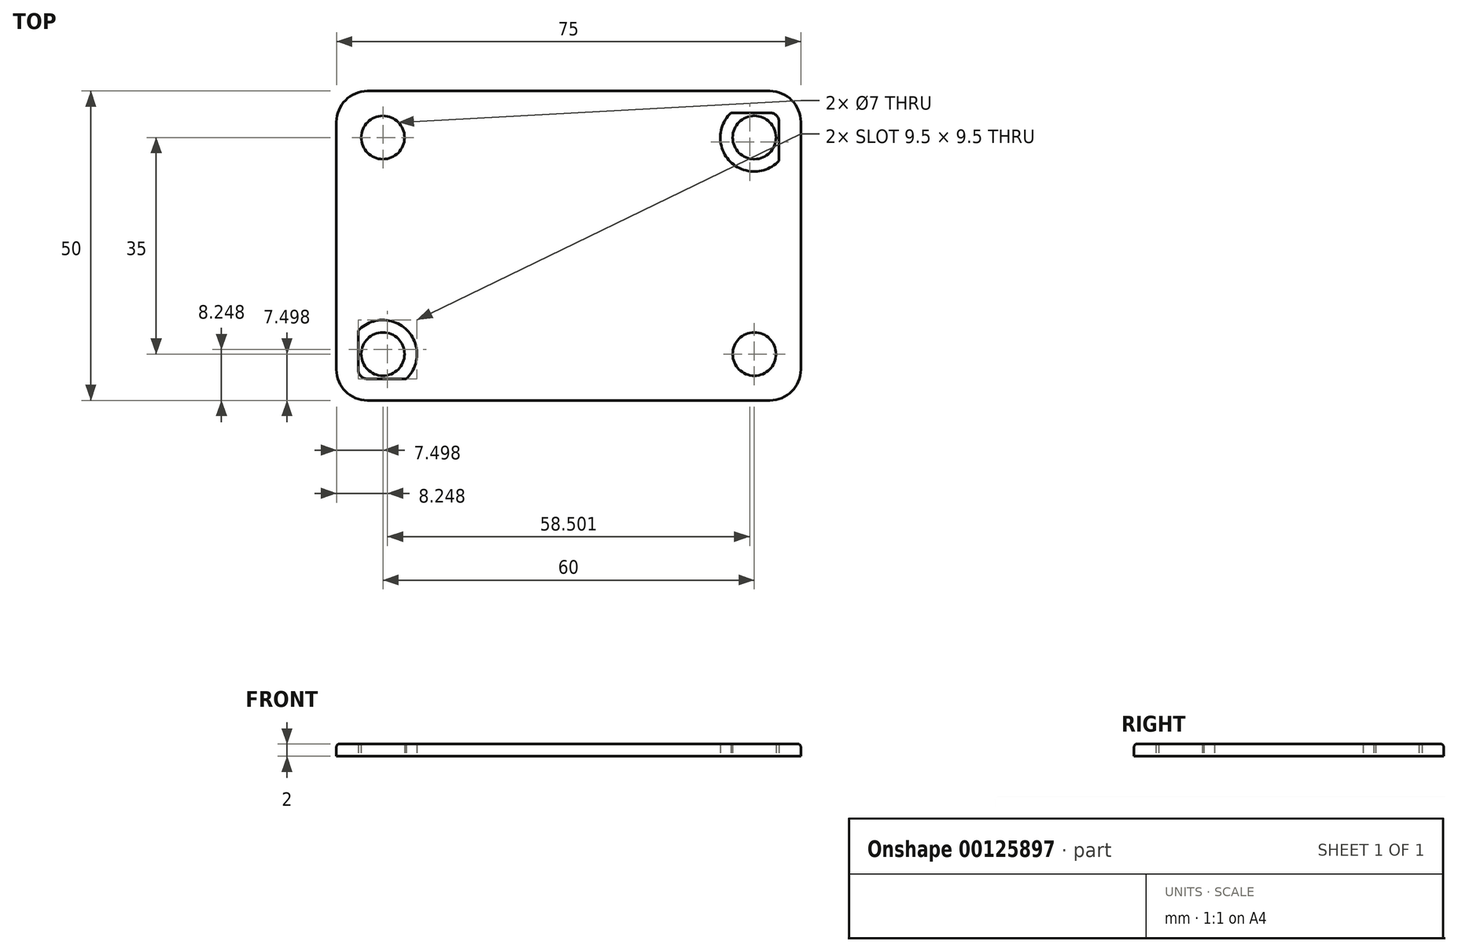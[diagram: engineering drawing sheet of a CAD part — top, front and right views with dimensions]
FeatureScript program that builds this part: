
annotation { "Feature Type Name" : "Feature", "Feature Type Description" : "" }
export const myFeature = defineFeature(function(context is Context, id is Id, definition is map)
    precondition{}
    {
        {
            var Q0;
            Q0=qCreatedBy(makeId("Top.planeOp"),FACE);
            var sketch = newSketch(context, id + "F0", { "sketchPlane" : qUnion([Q0])});
            skLineSegment(sketch, "E0.bottom", {"start": v(33.09, 25.59) * mm, "end": v(-31.91, 25.59) * mm});
            skLineSegment(sketch, "E0.top", {"start": v(33.09, -24.41) * mm, "end": v(-31.91, -24.41) * mm});
            skLineSegment(sketch, "E0.left", {"start": v(38.09, 20.59) * mm, "end": v(38.09, -19.41) * mm});
            skLineSegment(sketch, "E0.right", {"start": v(-36.91, 20.59) * mm, "end": v(-36.91, -19.41) * mm});
            skPoint(sketch, "E0.middle", {"position": v(0.59, 0.59) * mm});
            skCircle(sketch, "E1", {"center": v(-29.41, 18.09) * mm, "radius": 3.5 * mm});
            skLineSegment(sketch, "E2", {"start": v(0.59, 0.59) * mm, "end": v(0.59, 25.59) * mm, "construction": true});
            skLineSegment(sketch, "E3", {"start": v(0.59, 0.59) * mm, "end": v(0.59, -24.41) * mm, "construction": true});
            skLineSegment(sketch, "E4", {"start": v(0.59, 0.59) * mm, "end": v(38.09, 0.59) * mm, "construction": true});
            skLineSegment(sketch, "E5", {"start": v(0.59, 0.59) * mm, "end": v(-36.91, 0.59) * mm, "construction": true});
            skCircle(sketch, "E6.MirrorC", {"center": v(-29.41, -16.91) * mm, "radius": 3.5 * mm});
            skCircle(sketch, "E7.MirrorC", {"center": v(30.59, 18.09) * mm, "radius": 3.5 * mm});
            skCircle(sketch, "E8.MirrorC", {"center": v(30.59, -16.91) * mm, "radius": 3.5 * mm});
            skPoint(sketch, "E9.visualSharp", {"position": v(-36.91, 25.59) * mm});
            skArc(sketch, "E9.filletArc", {"start": v(-31.91, 25.59) * mm, "mid": v(-35.45, 24.12) * mm, "end": v(-36.91, 20.59) * mm});
            skPoint(sketch, "E10.visualSharp", {"position": v(38.09, 25.59) * mm});
            skArc(sketch, "E10.filletArc", {"start": v(38.09, 20.59) * mm, "mid": v(36.62, 24.12) * mm, "end": v(33.09, 25.59) * mm});
            skPoint(sketch, "E11.visualSharp", {"position": v(38.09, -24.41) * mm});
            skArc(sketch, "E11.filletArc", {"start": v(33.09, -24.41) * mm, "mid": v(36.62, -22.95) * mm, "end": v(38.09, -19.41) * mm});
            skPoint(sketch, "E12.visualSharp", {"position": v(-36.91, -24.41) * mm});
            skArc(sketch, "E12.filletArc", {"start": v(-36.91, -19.41) * mm, "mid": v(-35.45, -22.95) * mm, "end": v(-31.91, -24.41) * mm});
            skArc(sketch, "E13.0", {"start": v(37.09, 20.59) * mm, "mid": v(35.92, 23.42) * mm, "end": v(33.09, 24.59) * mm});
            skLineSegment(sketch, "E13.1", {"start": v(37.09, 20.59) * mm, "end": v(37.09, -19.41) * mm});
            skLineSegment(sketch, "E13.2", {"start": v(33.09, 24.59) * mm, "end": v(-31.91, 24.59) * mm});
            skArc(sketch, "E13.3", {"start": v(33.09, -23.41) * mm, "mid": v(35.92, -22.24) * mm, "end": v(37.09, -19.41) * mm});
            skArc(sketch, "E13.4", {"start": v(-31.91, 24.59) * mm, "mid": v(-34.74, 23.42) * mm, "end": v(-35.91, 20.59) * mm});
            skLineSegment(sketch, "E13.5", {"start": v(-35.91, 20.59) * mm, "end": v(-35.91, -19.41) * mm});
            skArc(sketch, "E13.6", {"start": v(-35.91, -19.41) * mm, "mid": v(-34.74, -22.24) * mm, "end": v(-31.91, -23.41) * mm});
            skLineSegment(sketch, "E13.7", {"start": v(33.09, -23.41) * mm, "end": v(-31.91, -23.41) * mm});
            skArc(sketch, "E14.0", {"start": v(35.59, 20.59) * mm, "mid": v(34.86, 22.36) * mm, "end": v(33.09, 23.09) * mm});
            skLineSegment(sketch, "E14.1", {"start": v(35.59, 20.59) * mm, "end": v(35.59, -19.41) * mm});
            skLineSegment(sketch, "E14.2", {"start": v(33.09, 23.09) * mm, "end": v(-31.91, 23.09) * mm});
            skArc(sketch, "E14.3", {"start": v(33.09, -21.91) * mm, "mid": v(34.86, -21.18) * mm, "end": v(35.59, -19.41) * mm});
            skArc(sketch, "E14.4", {"start": v(-31.91, 23.09) * mm, "mid": v(-33.68, 22.36) * mm, "end": v(-34.41, 20.59) * mm});
            skLineSegment(sketch, "E14.5", {"start": v(-34.41, 20.59) * mm, "end": v(-34.41, -19.41) * mm});
            skArc(sketch, "E14.6", {"start": v(-34.41, -19.41) * mm, "mid": v(-33.68, -21.18) * mm, "end": v(-31.91, -21.91) * mm});
            skLineSegment(sketch, "E14.7", {"start": v(33.09, -21.91) * mm, "end": v(-31.91, -21.91) * mm});
            skArc(sketch, "E15.0", {"start": v(34.59, 20.59) * mm, "mid": v(34.15, 21.65) * mm, "end": v(33.09, 22.09) * mm});
            skLineSegment(sketch, "E15.1", {"start": v(34.59, 20.59) * mm, "end": v(34.59, -19.41) * mm});
            skLineSegment(sketch, "E15.2", {"start": v(33.09, 22.09) * mm, "end": v(-31.91, 22.09) * mm});
            skArc(sketch, "E15.3", {"start": v(33.09, -20.91) * mm, "mid": v(34.15, -20.47) * mm, "end": v(34.59, -19.41) * mm});
            skArc(sketch, "E15.4", {"start": v(-31.91, 22.09) * mm, "mid": v(-32.97, 21.65) * mm, "end": v(-33.41, 20.59) * mm});
            skLineSegment(sketch, "E15.5", {"start": v(-33.41, 20.59) * mm, "end": v(-33.41, -19.41) * mm});
            skArc(sketch, "E15.6", {"start": v(-33.41, -19.41) * mm, "mid": v(-32.97, -20.47) * mm, "end": v(-31.91, -20.91) * mm});
            skLineSegment(sketch, "E15.7", {"start": v(33.09, -20.91) * mm, "end": v(-31.91, -20.91) * mm});
            skArc(sketch, "E16.0", {"start": v(-33.41, 14.31) * mm, "mid": v(-25.52, 14.2) * mm, "end": v(-25.64, 22.09) * mm});
            skArc(sketch, "E17.MirrorCS", {"start": v(34.59, 14.31) * mm, "mid": v(26.7, 14.2) * mm, "end": v(26.81, 22.09) * mm});
            skArc(sketch, "E18.MirrorCS", {"start": v(-33.41, -13.14) * mm, "mid": v(-25.52, -13.02) * mm, "end": v(-25.64, -20.91) * mm});
            skArc(sketch, "E19.MirrorCS", {"start": v(34.59, -13.14) * mm, "mid": v(26.7, -13.02) * mm, "end": v(26.81, -20.91) * mm});
            skSolve(sketch);
        }
        {
            var Q0;
            Q0=makeQuery(id+"F0.imprint","IMPRINT",FACE,{"disambiguationData":[TD([[makeQuery(id+"F0.imprint","IMPRINT",EDGE,{"derivedFrom":sQuery(id+"F0.wireOp",EDGE,"E14.0")}),1.0]])]});
            var Q1;
            Q1=makeQuery(id+"F0.imprint","IMPRINT",FACE,{"disambiguationData":[TD([[makeQuery(id+"F0.imprint","IMPRINT",EDGE,{"derivedFrom":sQuery(id+"F0.wireOp",EDGE,"E1")}),-1.0]])]});
            var Q2;
            Q2=makeQuery(id+"F0.imprint","IMPRINT",FACE,{"disambiguationData":[TD([[makeQuery(id+"F0.imprint","IMPRINT",EDGE,{"derivedFrom":sQuery(id+"F0.wireOp",EDGE,"E6.MirrorC")}),1.0]])]});
            var Q3;
            Q3=makeQuery(id+"F0.imprint","IMPRINT",FACE,{"disambiguationData":[TD([[makeQuery(id+"F0.imprint","IMPRINT",EDGE,{"derivedFrom":sQuery(id+"F0.wireOp",EDGE,"E7.MirrorC")}),1.0]])]});
            var Q4;
            Q4=makeQuery(id+"F0.imprint","IMPRINT",FACE,{"disambiguationData":[TD([[makeQuery(id+"F0.imprint","IMPRINT",EDGE,{"derivedFrom":sQuery(id+"F0.wireOp",EDGE,"E8.MirrorC")}),-1.0]])]});
            var Q5;
            Q5=makeQuery(id+"F0.imprint","IMPRINT",FACE,{"disambiguationData":[TD([[makeQuery(id+"F0.imprint","IMPRINT",EDGE,{"derivedFrom":sQuery(id+"F0.wireOp",EDGE,"E0.bottom")}),1.0]])]});
            var Q6;
            Q6=makeQuery(id+"F0.imprint","IMPRINT",FACE,{"disambiguationData":[TD([[makeQuery(id+"F0.imprint","IMPRINT",EDGE,{"derivedFrom":sQuery(id+"F0.wireOp",EDGE,"E13.0")}),1.0]])]});
            var Q7;
            {var subQ0=sQuery(id+"F0.wireOp",EDGE,"E16.0");Q7=makeQuery(id+"F0.imprint","IMPRINT",FACE,{"disambiguationData":[TD([[makeQuery(id+"F0.imprint","IMPRINT",EDGE,{"derivedFrom":subQ0}),-1.0]])]});}
            extrude(context, id + "F1", {"entities" : qUnion([Q0, Q1, Q2, Q3, Q4, Q5, Q6, Q7]), "depth" : 2 * mm});
        }
        {
            var Q0;
            Q0=makeQuery(id+"F1.opExtrude","CAP_EDGE",EDGE,{"disambiguationData":[OSD([sQuery(id+"F0.wireOp",EDGE,"E0.right")])],"isStart":false});
            fillet(context, id + "F2", {"entities" : qUnion([Q0]), "radius" : .5 * mm, "tangentPropagation" : true, "allowEdgeOverflow" : false});
        }
    });
